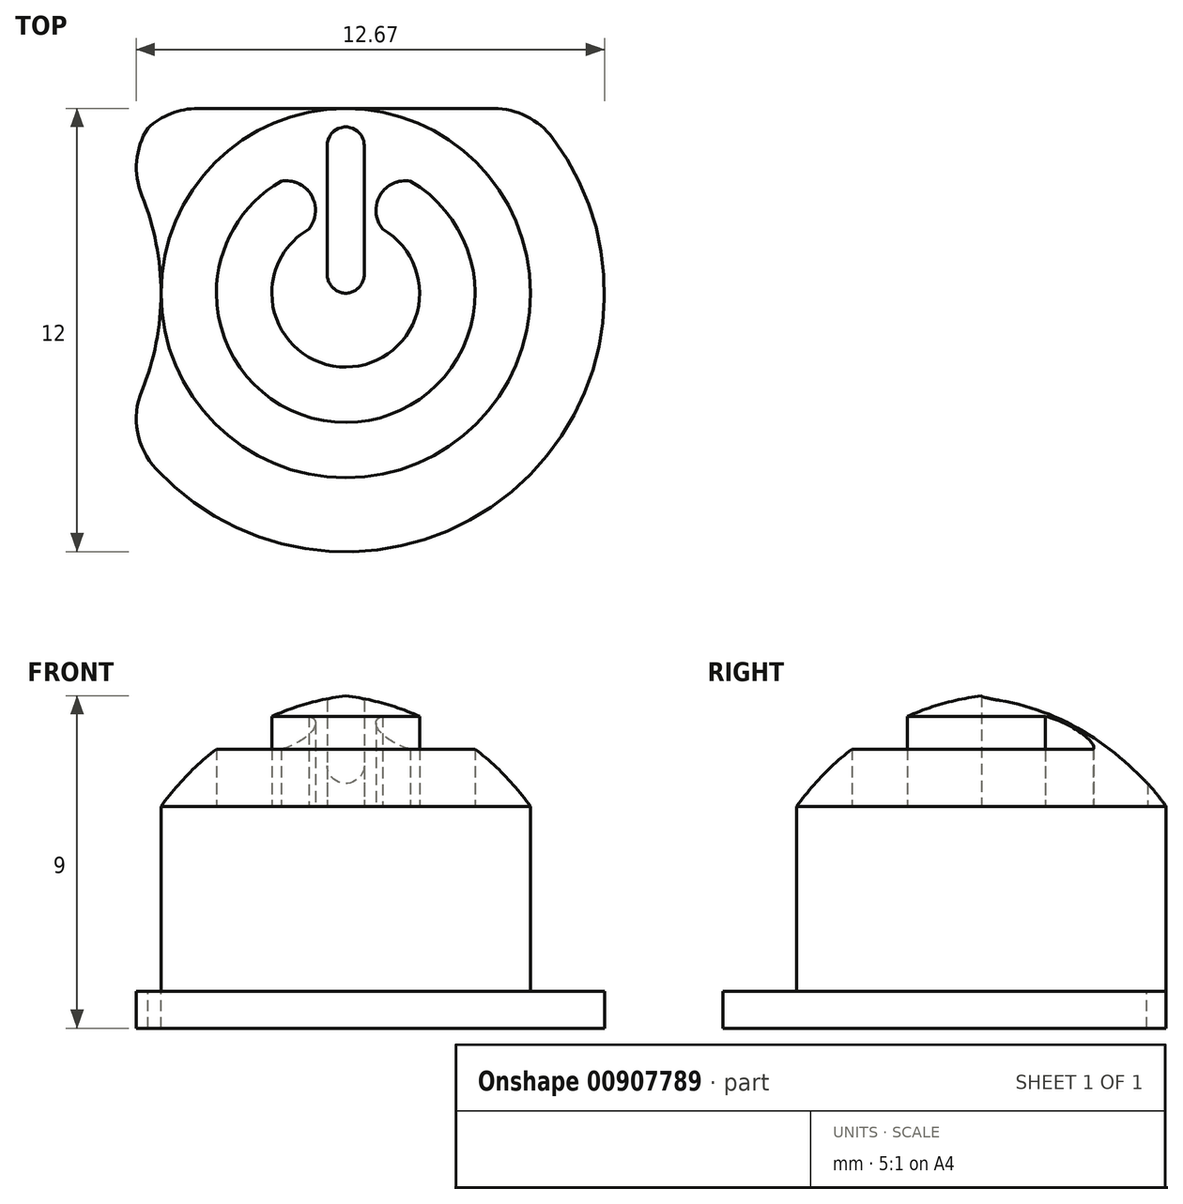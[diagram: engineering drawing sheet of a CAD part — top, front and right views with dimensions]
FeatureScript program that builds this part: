
annotation { "Feature Type Name" : "Feature", "Feature Type Description" : "" }
export const myFeature = defineFeature(function(context is Context, id is Id, definition is map)
    precondition{}
    {
        {
            var Q0;
            Q0=qCreatedBy(makeId("Front.planeOp"),FACE);
            var sketch = newSketch(context, id + "F0", { "sketchPlane" : qUnion([Q0])});
            skLineSegment(sketch, "E0.bottom", {"start": v(0, 0) * mm, "end": v(5, 0) * mm});
            skLineSegment(sketch, "E0.top", {"start": v(0, -5) * mm, "end": v(5, -5) * mm});
            skLineSegment(sketch, "E0.left", {"start": v(0, 0) * mm, "end": v(0, -5) * mm});
            skLineSegment(sketch, "E0.right", {"start": v(5, 0) * mm, "end": v(5, -5) * mm});
            skLineSegment(sketch, "E1", {"start": v(0, 0) * mm, "end": v(0, 3) * mm});
            skArc(sketch, "E2.trimOffspring", {"start": v(5, 0) * mm, "mid": v(2.81, 2.02) * mm, "end": v(0, 3) * mm});
            skLineSegment(sketch, "E3.bottom", {"start": v(0, -5) * mm, "end": v(7, -5) * mm});
            skLineSegment(sketch, "E3.top", {"start": v(0, -6) * mm, "end": v(7, -6) * mm});
            skLineSegment(sketch, "E3.left", {"start": v(0, -5) * mm, "end": v(0, -6) * mm});
            skLineSegment(sketch, "E3.right", {"start": v(7, -5) * mm, "end": v(7, -6) * mm});
            skSolve(sketch);
        }
        {
            var Q0;
            Q0=makeQuery(id+"F0.imprint","IMPRINT",FACE,{"disambiguationData":[TD([[makeQuery(id+"F0.imprint","IMPRINT",EDGE,{"derivedFrom":sQuery(id+"F0.wireOp",EDGE,"E0.bottom")}),1.0]])]});
            var Q1;
            Q1=makeQuery(id+"F0.imprint","IMPRINT",FACE,{"disambiguationData":[TD([[makeQuery(id+"F0.imprint","IMPRINT",EDGE,{"derivedFrom":sQuery(id+"F0.wireOp",EDGE,"E0.bottom")}),-1.0]])]});
            var Q2;
            Q2=makeQuery(id+"F0.imprint","IMPRINT",FACE,{"disambiguationData":[TD([[makeQuery(id+"F0.imprint","IMPRINT",EDGE,{"derivedFrom":sQuery(id+"F0.wireOp",EDGE,"E3.top")}),1.0]])]});
            var Q3;
            Q3=sQuery(id+"F0.wireOp",EDGE,"E0.left");
            revolve(context, id + "F1", {"surfaceOperationType" : NewSurfaceOperationType.NEW, "entities" : qUnion([Q0, Q1, Q2]), "axis" : qUnion([Q3]), "revolveType" : RevolveType.FULL});
        }
        {
            var Q0;
            Q0=makeQuery(id+"F1.opRevolve","SWEPT_FACE",FACE,{"disambiguationData":[OSD([sQuery(id+"F0.wireOp",EDGE,"E3.bottom")])]});
            cPlane(context, id + "F2", {"entities" : qUnion([Q0]), "cplaneType" : CPlaneType.OFFSET, "offset" : 5 * mm, "width" : 150 * mm, "height" : 150 * mm});
        }
        {
            var Q0;
            Q0=qCreatedBy(id+"F2.planeOp",FACE);
            var sketch = newSketch(context, id + "F3", { "sketchPlane" : qUnion([Q0])});
            skArc(sketch, "E4", {"start": v(-1.75, 3.03) * mm, "mid": v(0, -3.5) * mm, "end": v(1.75, 3.03) * mm});
            skArc(sketch, "E5", {"start": v(-1, 1.73) * mm, "mid": v(0, -2) * mm, "end": v(1, 1.73) * mm});
            skLineSegment(sketch, "E6", {"start": v(-1, 1.73) * mm, "end": v(-1.75, 3.03) * mm});
            skLineSegment(sketch, "E7", {"start": v(1, 1.73) * mm, "end": v(1.75, 3.03) * mm});
            skLineSegment(sketch, "E8", {"start": v(0, 0) * mm, "end": v(0, 2) * mm});
            skArc(sketch, "E9", {"start": v(-1, 1.73) * mm, "mid": v(-0.92, 2.64) * mm, "end": v(-1.75, 3.03) * mm});
            skArc(sketch, "E10", {"start": v(1.75, 3.03) * mm, "mid": v(0.92, 2.64) * mm, "end": v(1, 1.73) * mm});
            skLineSegment(sketch, "E11.bottom", {"start": v(0.5, 0.5) * mm, "end": v(-0.5, 0.5) * mm});
            skLineSegment(sketch, "E11.top", {"start": v(0.5, 4) * mm, "end": v(-0.5, 4) * mm});
            skLineSegment(sketch, "E11.left", {"start": v(0.5, 0.5) * mm, "end": v(0.5, 4) * mm});
            skLineSegment(sketch, "E11.right", {"start": v(-0.5, 0.5) * mm, "end": v(-0.5, 4) * mm});
            skPoint(sketch, "E11.middle", {"position": v(0, 2.25) * mm});
            skArc(sketch, "E12", {"start": v(0.5, 4) * mm, "mid": v(0, 4.5) * mm, "end": v(-0.5, 4) * mm});
            skArc(sketch, "E13", {"start": v(-0.5, 0.5) * mm, "mid": v(0, 0) * mm, "end": v(0.5, 0.5) * mm});
            skSolve(sketch);
        }
        {
            var Q0;
            Q0 = qSketchRegion(id + "F3", true);
            extrude(context, id + "F4", {"entities" : qUnion([Q0]), "operationType" : NewBodyOperationType.REMOVE, "endBound" : BoundingType.THROUGH_ALL, "depth" : 2 * mm, "offsetDistance" : 25 * mm});
        }
        {
            var Q0;
            Q0=makeQuery(id+"F1.opRevolve","SWEPT_FACE",FACE,{"disambiguationData":[OSD([sQuery(id+"F0.wireOp",EDGE,"E3.bottom")])]});
            var sketch = newSketch(context, id + "F5", { "sketchPlane" : qUnion([Q0])});
            skLineSegment(sketch, "E14", {"start": v(0, 5) * mm, "end": v(8.99, 5) * mm});
            skLineSegment(sketch, "E15", {"start": v(8.99, 5) * mm, "end": v(8.99, 8.45) * mm});
            skLineSegment(sketch, "E16", {"start": v(8.99, 8.45) * mm, "end": v(-9.46, 8.45) * mm});
            skLineSegment(sketch, "E17", {"start": v(-9.46, 8.45) * mm, "end": v(-9.46, 5) * mm});
            skLineSegment(sketch, "E18", {"start": v(-9.46, 5) * mm, "end": v(0, 5) * mm});
            skPoint(sketch, "E19", {"position": v(-5, 0) * mm});
            skCircle(sketch, "E20", {"center": v(-12, 0) * mm, "radius": 7 * mm});
            skSolve(sketch);
        }
        {
            var Q0;
            Q0 = qSketchRegion(id + "F5", true);
            extrude(context, id + "F6", {"entities" : qUnion([Q0]), "operationType" : NewBodyOperationType.REMOVE, "endBound" : BoundingType.THROUGH_ALL, "oppositeDirection" : true, "depth" : 25 * mm, "offsetDistance" : 25 * mm});
        }
        {
            var Q0;
            Q0=makeQuery(id+"F6.boolean.opBoolean","INTERSECT",EDGE,{"disambiguationData":[OD(1.0)],"derivedFrom":[makeQuery(id+"F1.opRevolve","SWEPT_FACE",FACE,{"disambiguationData":[OSD([sQuery(id+"F0.wireOp",EDGE,"E3.right")])]}),makeQuery(id+"F6.opExtrude","SWEPT_FACE",FACE,{"disambiguationData":[OSD([sQuery(id+"F5.wireOp",EDGE,"E20")])]})]});
            var Q1;
            Q1=makeQuery(id+"F6.boolean.opBoolean","INTERSECT",EDGE,{"disambiguationData":[OD(0.0)],"derivedFrom":[makeQuery(id+"F1.opRevolve","SWEPT_FACE",FACE,{"disambiguationData":[OSD([sQuery(id+"F0.wireOp",EDGE,"E3.right")])]}),makeQuery(id+"F6.opExtrude","SWEPT_FACE",FACE,{"disambiguationData":[OSD([sQuery(id+"F5.wireOp",EDGE,"E20")])]})]});
            var Q2;
            Q2=makeQuery(id+"F6.boolean.opBoolean","INTERSECT",EDGE,{"disambiguationData":[OD(0.0)],"derivedFrom":[makeQuery(id+"F1.opRevolve","SWEPT_FACE",FACE,{"disambiguationData":[OSD([sQuery(id+"F0.wireOp",EDGE,"E3.right")])]}),makeQuery(id+"F6.opExtrude","SWEPT_FACE",FACE,{"disambiguationData":[OSD([sQuery(id+"F5.wireOp",EDGE,"E14"),sQuery(id+"F5.wireOp",EDGE,"E18")])]})]});
            var Q3;
            Q3=makeQuery(id+"F6.boolean.opBoolean","INTERSECT",EDGE,{"disambiguationData":[OD(1.0)],"derivedFrom":[makeQuery(id+"F1.opRevolve","SWEPT_FACE",FACE,{"disambiguationData":[OSD([sQuery(id+"F0.wireOp",EDGE,"E3.right")])]}),makeQuery(id+"F6.opExtrude","SWEPT_FACE",FACE,{"disambiguationData":[OSD([sQuery(id+"F5.wireOp",EDGE,"E14"),sQuery(id+"F5.wireOp",EDGE,"E18")])]})]});
            fillet(context, id + "F7", {"entities" : qUnion([Q0, Q1, Q2, Q3]), "radius" : 2 * mm, "tangentPropagation" : true, "allowEdgeOverflow" : false});
        }
    });
